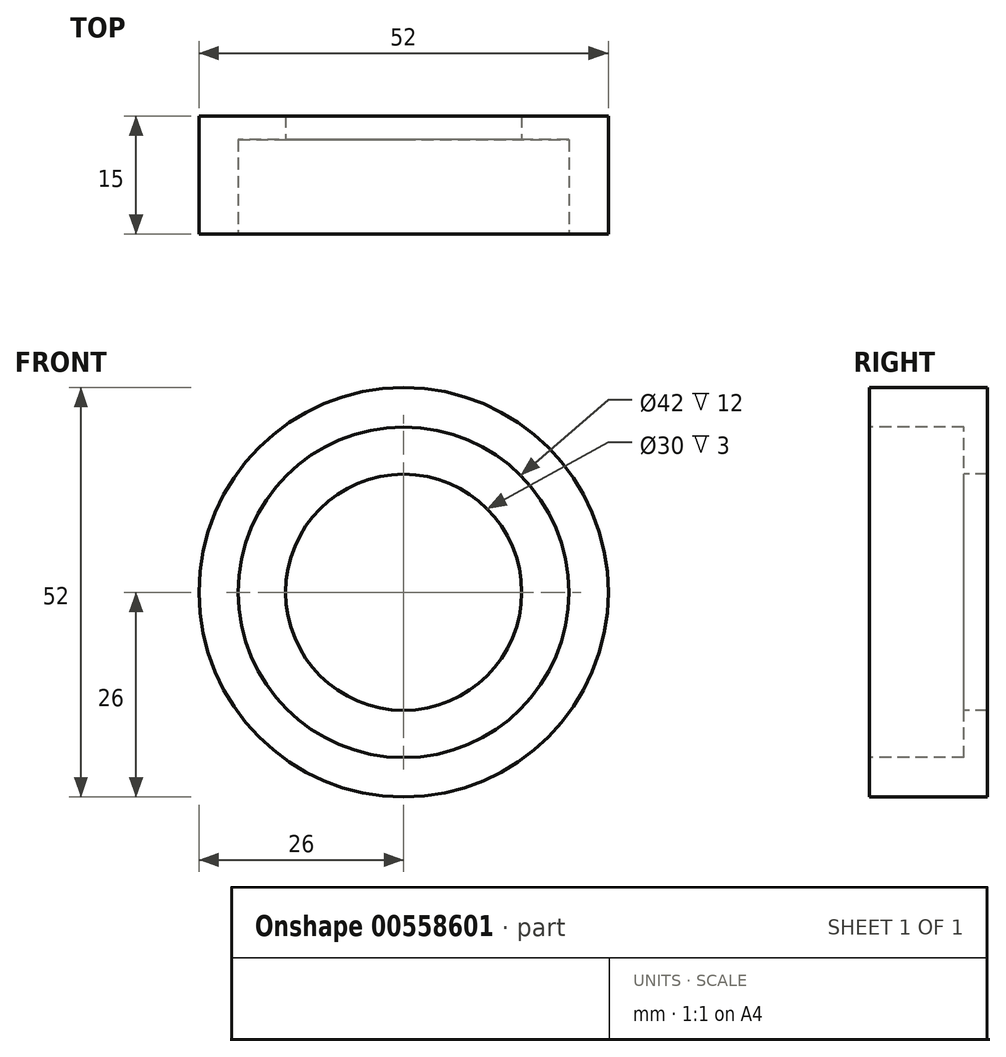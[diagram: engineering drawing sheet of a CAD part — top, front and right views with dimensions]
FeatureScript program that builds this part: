
annotation { "Feature Type Name" : "Feature", "Feature Type Description" : "" }
export const myFeature = defineFeature(function(context is Context, id is Id, definition is map)
    precondition{}
    {
        {
            var Q0;
            Q0=qCreatedBy(makeId("Front.planeOp"),FACE);
            var sketch = newSketch(context, id + "F0", { "sketchPlane" : qUnion([Q0])});
            skCircle(sketch, "E0", {"center": v(0, 0) * mm, "radius": 26 * mm});
            skSolve(sketch);
        }
        {
            var Q0;
            Q0 = qSketchRegion(id + "F0", true);
            extrude(context, id + "F1", {"entities" : qUnion([Q0]), "depth" : 15 * mm, "offsetDistance" : 25 * mm});
        }
        {
            var Q0;
            Q0=makeQuery(id+"F1.opExtrude","CAP_FACE",FACE,{"disambiguationData":[OSD([sQuery(id+"F0.wireOp",EDGE,"E0")])],"isStart":false});
            var sketch = newSketch(context, id + "F2", { "sketchPlane" : qUnion([Q0])});
            skSolve(sketch);
        }
        {
            var Q0;
            Q0=makeQuery(id+"F2.imprint","IMPRINT",FACE,{"disambiguationData":[TD([[makeQuery(id+"F2.imprint","IMPRINT",EDGE,{"derivedFrom":makeQuery(id+"F1.opExtrude","CAP_EDGE",EDGE,{"disambiguationData":[OSD([sQuery(id+"F0.wireOp",EDGE,"E0")])],"isStart":false})}),1.0]])]});
            var sketch = newSketch(context, id + "F3", { "sketchPlane" : qUnion([Q0])});
            skCircle(sketch, "E1", {"center": v(0, 0) * mm, "radius": 21 * mm});
            skSolve(sketch);
        }
        {
            var Q0;
            Q0 = qSketchRegion(id + "F3", true);
            extrude(context, id + "F4", {"entities" : qUnion([Q0]), "operationType" : NewBodyOperationType.REMOVE, "oppositeDirection" : true, "depth" : 12 * mm, "offsetDistance" : 25 * mm});
        }
        {
            var Q0;
            Q0=makeQuery(id+"F2.imprint","IMPRINT",FACE,{"disambiguationData":[TD([[makeQuery(id+"F2.imprint","IMPRINT",EDGE,{"derivedFrom":makeQuery(id+"F1.opExtrude","CAP_EDGE",EDGE,{"disambiguationData":[OSD([sQuery(id+"F0.wireOp",EDGE,"E0")])],"isStart":false})}),1.0]])]});
            var sketch = newSketch(context, id + "F5", { "sketchPlane" : qUnion([Q0])});
            skCircle(sketch, "E2", {"center": v(0, 0) * mm, "radius": 15 * mm});
            skSolve(sketch);
        }
        {
            var Q0;
            Q0 = qSketchRegion(id + "F5", true);
            extrude(context, id + "F6", {"entities" : qUnion([Q0]), "operationType" : NewBodyOperationType.REMOVE, "oppositeDirection" : true, "depth" : 25 * mm, "offsetDistance" : 25 * mm});
        }
    });
